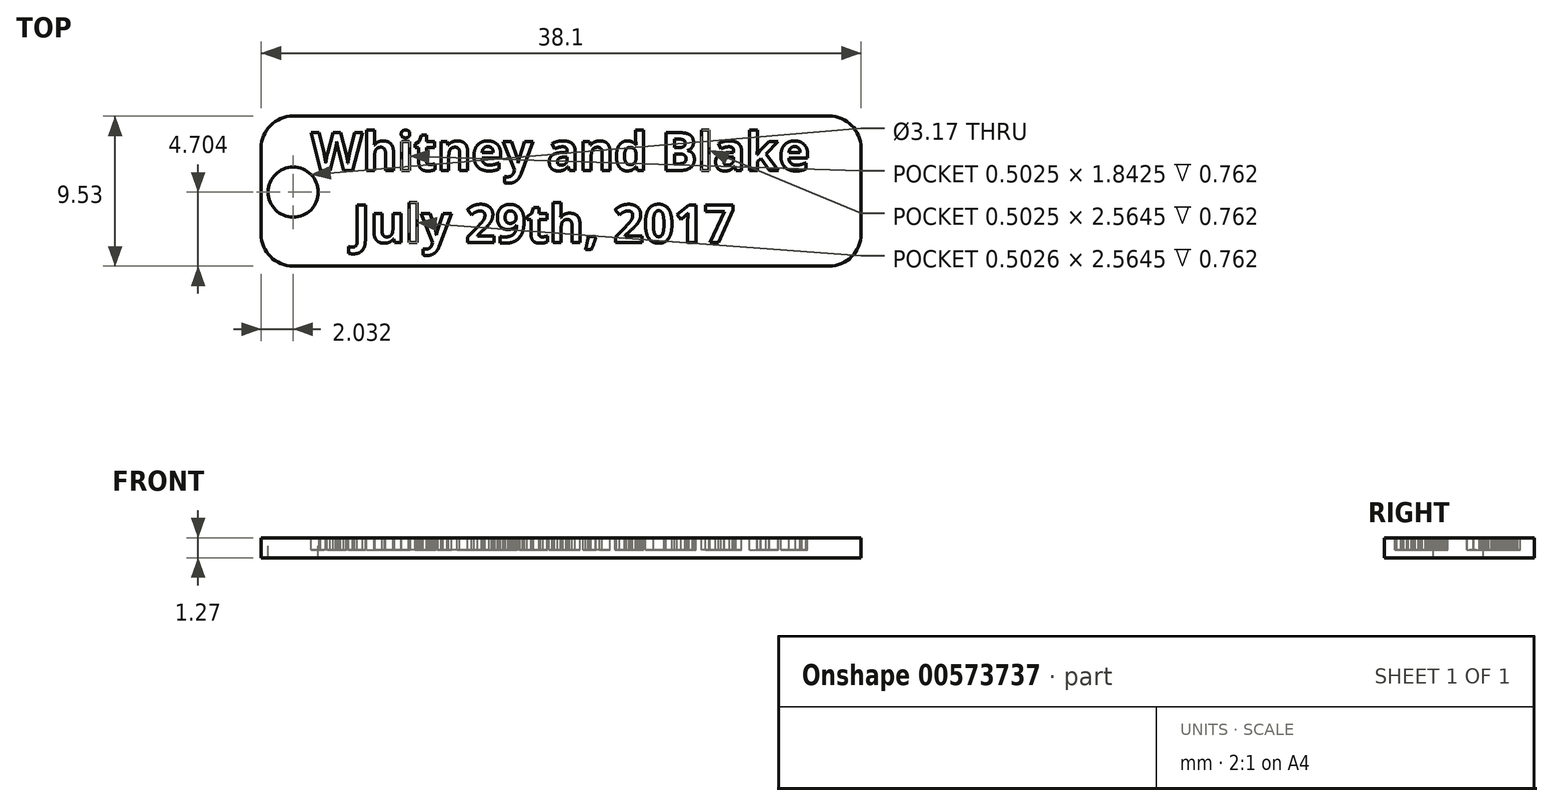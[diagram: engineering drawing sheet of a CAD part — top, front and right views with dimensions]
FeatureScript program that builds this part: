
annotation { "Feature Type Name" : "Feature", "Feature Type Description" : "" }
export const myFeature = defineFeature(function(context is Context, id is Id, definition is map)
    precondition{}
    {
        {
            var Q0;
            Q0=qCreatedBy(makeId("Top.planeOp"),FACE);
            var sketch = newSketch(context, id + "F0", { "sketchPlane" : qUnion([Q0])});
            skLineSegment(sketch, "E0.bottom", {"start": v(0, 0) * mm, "end": v(38.1, 0) * mm});
            skLineSegment(sketch, "E0.top", {"start": v(0, -9.53) * mm, "end": v(38.1, -9.53) * mm});
            skLineSegment(sketch, "E0.left", {"start": v(0, 0) * mm, "end": v(0, -9.53) * mm});
            skLineSegment(sketch, "E0.right", {"start": v(38.1, 0) * mm, "end": v(38.1, -9.53) * mm});
            skSolve(sketch);
        }
        {
            var Q0;
            Q0=makeQuery(id+"F0.imprint","IMPRINT",FACE,{"disambiguationData":[TD([[makeQuery(id+"F0.imprint","IMPRINT",EDGE,{"derivedFrom":sQuery(id+"F0.wireOp",EDGE,"E0.bottom")}),-1.0]])]});
            extrude(context, id + "F1", {"entities" : qUnion([Q0]), "depth" : 1.27 * mm, "offsetDistance" : 25.4 * mm});
        }
        {
            var Q0;
            Q0=makeQuery(id+"F1.opExtrude","CAP_FACE",FACE,{"disambiguationData":[OSD([sQuery(id+"F0.wireOp",EDGE,"E0.bottom"),sQuery(id+"F0.wireOp",EDGE,"E0.top"),sQuery(id+"F0.wireOp",EDGE,"E0.left"),sQuery(id+"F0.wireOp",EDGE,"E0.right")])],"isStart":false});
            var sketch = newSketch(context, id + "F2", { "sketchPlane" : qUnion([Q0])});
            skText(sketch, "E1", { "text": "Whitney and Blake\n   July 29th, 2017", "fontName": "OpenSans-Bold.ttf"});
            const initialGuessF2  = {"E1": [0.00317, -0.00345, 1, 0, 0.00243]};
            skSetInitialGuess(sketch, initialGuessF2);
            skSolve(sketch);
        }
        {
            var Q0;
            Q0 = qSketchRegion(id + "F2", true);
            extrude(context, id + "F3", {"entities" : qUnion([Q0]), "operationType" : NewBodyOperationType.REMOVE, "oppositeDirection" : true, "depth" : 0.76 * mm, "offsetDistance" : 25.4 * mm});
        }
        {
            var Q0;
            {var subQ0=sQuery(id+"F0.wireOp",EDGE,"E0.right");var subQ1=sQuery(id+"F0.wireOp",EDGE,"E0.left");var subQ2=sQuery(id+"F0.wireOp",EDGE,"E0.top");var subQ3=sQuery(id+"F0.wireOp",EDGE,"E0.bottom");Q0=makeQuery(id+"F3.boolean.opBoolean","SPLIT",FACE,{"disambiguationData":[TD([makeQuery(id+"F1.opExtrude","SWEPT_FACE",FACE,{"disambiguationData":[OSD([subQ3])]})])],"derivedFrom":makeQuery(id+"F1.opExtrude","CAP_FACE",FACE,{"disambiguationData":[OSD([subQ3,subQ2,subQ1,subQ0])],"isStart":false})});}
            var sketch = newSketch(context, id + "F4", { "sketchPlane" : qUnion([Q0])});
            skCircle(sketch, "E2", {"center": v(2.03, -4.83) * mm, "radius": 1.59 * mm});
            skSolve(sketch);
        }
        {
            var Q0;
            Q0=makeQuery(id+"F4.imprint","IMPRINT",FACE,{"disambiguationData":[TD([[makeQuery(id+"F4.imprint","IMPRINT",EDGE,{"derivedFrom":sQuery(id+"F4.wireOp",EDGE,"E2")}),1.0]])]});
            extrude(context, id + "F5", {"entities" : qUnion([Q0]), "operationType" : NewBodyOperationType.REMOVE, "endBound" : BoundingType.UP_TO_NEXT, "oppositeDirection" : true, "depth" : 25.4 * mm, "offsetDistance" : 25.4 * mm});
        }
        {
            var Q0;
            Q0=makeQuery(id+"F1.opExtrude","SWEPT_EDGE",EDGE,{"disambiguationData":[OSD([sQuery(id+"F0.wireOp",EDGE,"E0.top"),sQuery(id+"F0.wireOp",EDGE,"E0.right")])]});
            var Q1;
            Q1=makeQuery(id+"F1.opExtrude","SWEPT_EDGE",EDGE,{"disambiguationData":[OSD([sQuery(id+"F0.wireOp",EDGE,"E0.bottom"),sQuery(id+"F0.wireOp",EDGE,"E0.right")])]});
            var Q2;
            Q2=makeQuery(id+"F1.opExtrude","SWEPT_EDGE",EDGE,{"disambiguationData":[OSD([sQuery(id+"F0.wireOp",EDGE,"E0.bottom"),sQuery(id+"F0.wireOp",EDGE,"E0.left")])]});
            var Q3;
            Q3=makeQuery(id+"F1.opExtrude","SWEPT_EDGE",EDGE,{"disambiguationData":[OSD([sQuery(id+"F0.wireOp",EDGE,"E0.top"),sQuery(id+"F0.wireOp",EDGE,"E0.left")])]});
            fillet(context, id + "F6", {"entities" : qUnion([Q0, Q1, Q2, Q3]), "radius" : 2.02 * mm, "tangentPropagation" : true, "allowEdgeOverflow" : false});
        }
    });
